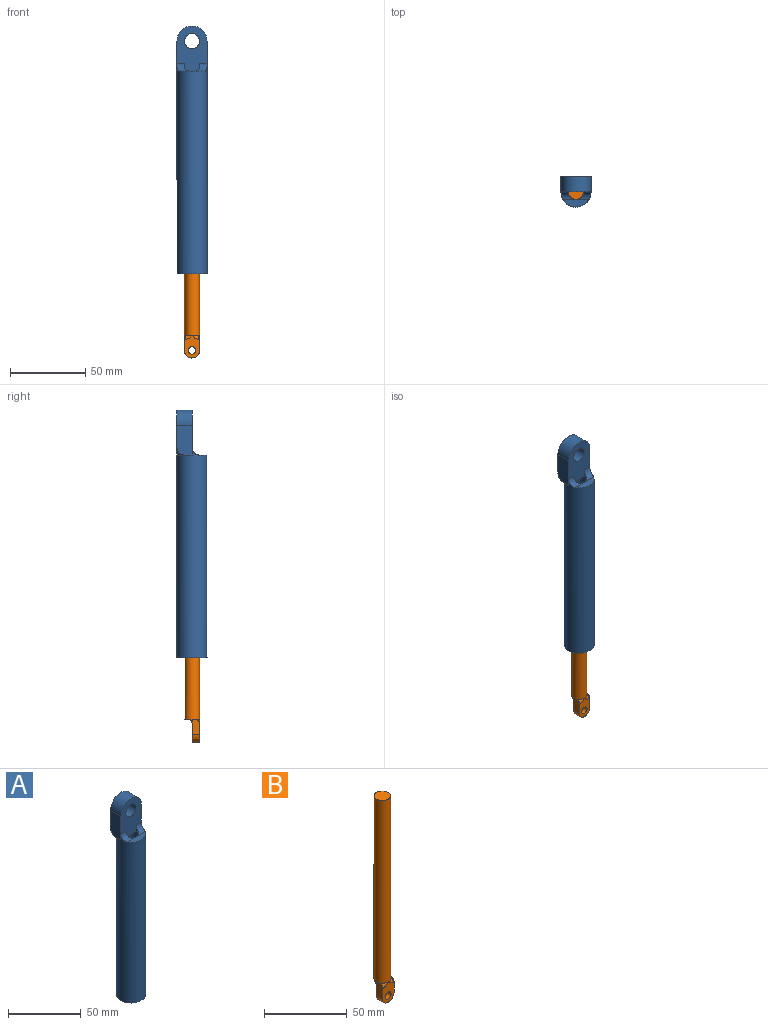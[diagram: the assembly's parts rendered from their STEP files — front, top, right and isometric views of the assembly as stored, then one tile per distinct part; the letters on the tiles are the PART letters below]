
ASSEMBLY  parts=2 mates=1
PART A: 19 faces, bbox 20x20x165 mm
  f0: cylinder r=5mm len=140mm, axis (0,0,1), area 4252.5mm2, adj f1,f5,f12,f15,f16
  f1: plane 20x20mm, normal (0,0,-1), area 235.6mm2, adj f0,f2
  f2: cylinder r=10mm len=140mm, axis (0,0,1), area 8493.2mm2, adj f1,f3,f4,f6,f8,f9,f14,f15
  f3: plane 17.32x5mm, normal (0,0,1), area 61.4mm2, adj f2,f15,f16
  f4: plane 5x1.34mm, normal (0,0,-1), area 2.2mm2, adj f2,f6,f13
  f5: plane 10x5mm, normal (0,0,-1), area 39.3mm2, adj f0,f12
  f6: plane 20x10mm, normal (1,0,0), area 194.6mm2, adj f2,f4,f7,f11,f12,f13
  f7: cylinder r=10mm len=20mm, axis (0,-1,0), area 314.2mm2, adj f6,f8,f11,f12
  f8: plane 20x10mm, normal (-1,0,0), area 194.6mm2, adj f2,f7,f9,f11,f12,f18
  f9: plane 5x1.34mm, normal (0,0,-1), area 2.2mm2, adj f2,f8,f18
  f10: cylinder r=5mm len=10mm, axis (0,-1,0), area 314.2mm2, adj f11,f12
  f11: plane 30x20mm, normal (0,1,0), area 408.4mm2, adj f6,f7,f8,f10,f13,f14,f17,f18
  f12: plane 30x20mm, normal (0,-1,0), area 428.5mm2, adj f0,f5,f6,f7,f8,f10,f15,f16
  f13: cylinder r=5mm len=5mm, axis (-1,0,0), area 10.5mm2, adj f4,f6,f11,f14
  f14: bspline ~9.72x5.45mm, area 33.6mm2, adj f2,f11,f13
  f15: cylinder r=5mm len=10mm, axis (-1,0,0), area 39.7mm2, adj f0,f2,f3,f12
  f16: cylinder r=5mm len=10mm, axis (-1,0,0), area 39.7mm2, adj f0,f2,f3,f12
  f17: bspline ~9.72x5.45mm, area 33.6mm2, adj f2,f11,f18
  f18: cylinder r=5mm len=5mm, axis (-1,0,0), area 10.5mm2, adj f8,f9,f11,f17
PART B: 16 faces, bbox 10.1x10.1x150.1 mm
  f0: cylinder r=5mm len=137.5mm, axis (0,0,-1), area 4243.9mm2, adj f1,f2,f3,f4,f5,f7,f12,f13
  f1: plane 10x10mm, normal (0,0,1), area 78.5mm2, adj f0
  f2: plane 8.66x2.5mm, normal (0,0,-1), area 15.4mm2, adj f0,f13
  f3: plane 2.5x0.67mm, normal (0,0,1), area 0.5mm2, adj f0,f7,f11
  f4: plane 2.5x0.67mm, normal (0,0,1), area 0.5mm2, adj f0,f5,f15
  f5: plane 10x5mm, normal (-1,0,0), area 48.7mm2, adj f0,f4,f6,f9,f10,f15
  f6: cylinder r=5mm len=10mm, axis (0,1,0), area 78.5mm2, adj f5,f7,f9,f10
  f7: plane 10x5mm, normal (1,0,0), area 48.7mm2, adj f0,f3,f6,f9,f10,f11
  f8: cylinder r=2.5mm len=5mm, axis (0,1,0), area 78.5mm2, adj f9,f10
  f9: plane 15.11x10.11mm, normal (0,-1,0), area 102.1mm2, adj f5,f6,f7,f8,f11,f12,f14,f15
  f10: plane 12.5x10mm, normal (0,1,0), area 94.6mm2, adj f5,f6,f7,f8,f13
  f11: cylinder r=2.5mm len=2.5mm, axis (1,0,0), area 2.6mm2, adj f3,f7,f9,f12
  f12: bspline ~4.86x2.73mm, area 8.2mm2, adj f0,f9,f11
  f13: cylinder r=2.5mm len=10mm, axis (1,0,0), area 36.6mm2, adj f0,f2,f10
  f14: bspline ~4.86x2.73mm, area 8.4mm2, adj f0,f9,f15
  f15: cylinder r=2.5mm len=2.5mm, axis (1,0,0), area 2.6mm2, adj f4,f5,f9,f14
PLACE A t=(-16.57,34.39,120.29)mm
PLACE B t=(-16.57,34.39,81.89)mm
MATE slider A.f0 <-> B.f0  axis (0,0,-1) through (50.51,34.39,-1.16)mm
